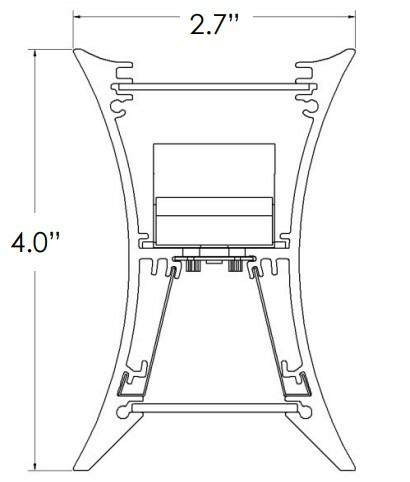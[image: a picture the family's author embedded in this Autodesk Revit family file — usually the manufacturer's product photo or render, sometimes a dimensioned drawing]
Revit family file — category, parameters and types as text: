
# Revit family: x directt
name_source: partatom
category: Lighting Fixtures
units: mm (PartAtom-declared; Revit-internal decimal feet)

## family parameters
Cut with Voids When Loaded = No
Host = Face
Light Source = Yes
OmniClass Number = 23.80.70.11
OmniClass Title = Luminaries for Internal Lighting
Part Type = Normal
Room Calculation Point = No
Round Connector Dimension = Use Diameter
Shared = No

## types (1)
- Not a type - Load Type Catalog!
    Apparent Load = 0 VA
    Assembly Code = D5020200
    CRI = 80
    Color Filter = 16777215
    Default Elevation = 4' - 0"
    Description = X-Beam Direct
    Dimming Lamp Color Temperature Shift = <None>
    Edition number = 1
    Emit Shape Visible in Rendering = No
    Frequency = 60 Hz
    Height = 0' - 4"
    Input Wattage = 0 W
    Keynote = 16500
    Lamp = LED
    Length = 4' - 0"
    Manufacturer = StarTek Lighting
    Number of Poles = 3
    Phase = 1
    Photometric Note = Import IES files https://starteklightingamerica.com
    Photometric Web File = Generic Light Source Shown : Please download and link the IES file that best matches your fixture specification
    Power Factor = 0.93
    Product Guid = 5de31e25-22b3-4453-9b70-2276e28f091a
    Product data url = https://www.bimobject.com
    Type Comments = Linear Lighting Fixture
    URL = https://starteklightingamerica.com
    Voltage = 120 V
    Voltage Range = 120-277V
    Wattage Comments = Efficacy up to 125 lm/W
    Weight = 0.00 lbf
    Width = 0' - 2 1/2"
    z_AC05 = Aircraft Cable : with Canopy 5' (AC05)
    z_AC10 = Aircraft Cable : with Canopy 10' (AC10)
    z_AL10 = Aircraft Cable : with Loops 10' (AL10)
    z_End = Run : End Fixture
    z_Middle = Run : Middle Fixture
    z_Standalone = Run : Standalone Fixture
    z_Start = Run : Start Fixture

## geometry (parser evidence)
native form markers: Sweep x10
no freeform markers — native parametric forms only
